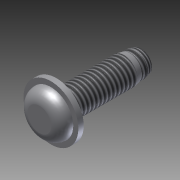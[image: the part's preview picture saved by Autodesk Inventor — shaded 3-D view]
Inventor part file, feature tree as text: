
AUTODESK INVENTOR PART (.ipt)
format: ipt  version: 2011 (Build 150239000, 239)  size: 165,888 bytes
history: native  units: in
note: dims shown in document units (in); Inventor stores cm internally (conversion verified against a paired STEP export)
features: thread x6, imported_body x1
ambient origin geometry x8: Origin, YZ Plane, XZ Plane, XY Plane, X Axis, Y Axis, Z Axis, Center Point
bodies: Solid1 (feature_tree)
feature tree (7):
  imported_body  "Base1"
  thread  "Thread1"  [1 undecoded]
  thread  "Thread2"  [1 undecoded]
  thread  "Thread3"  [1 undecoded]
  thread  "Thread4"  [1 undecoded]
  thread  "Thread5"  [1 undecoded]
  thread  "Thread6"  [1 undecoded]
note: 6 required parameter values undecoded (feature->parameter linkage not recoverable at this tier; creation-order binding heuristic only, values carry confidence <= 0.55)
